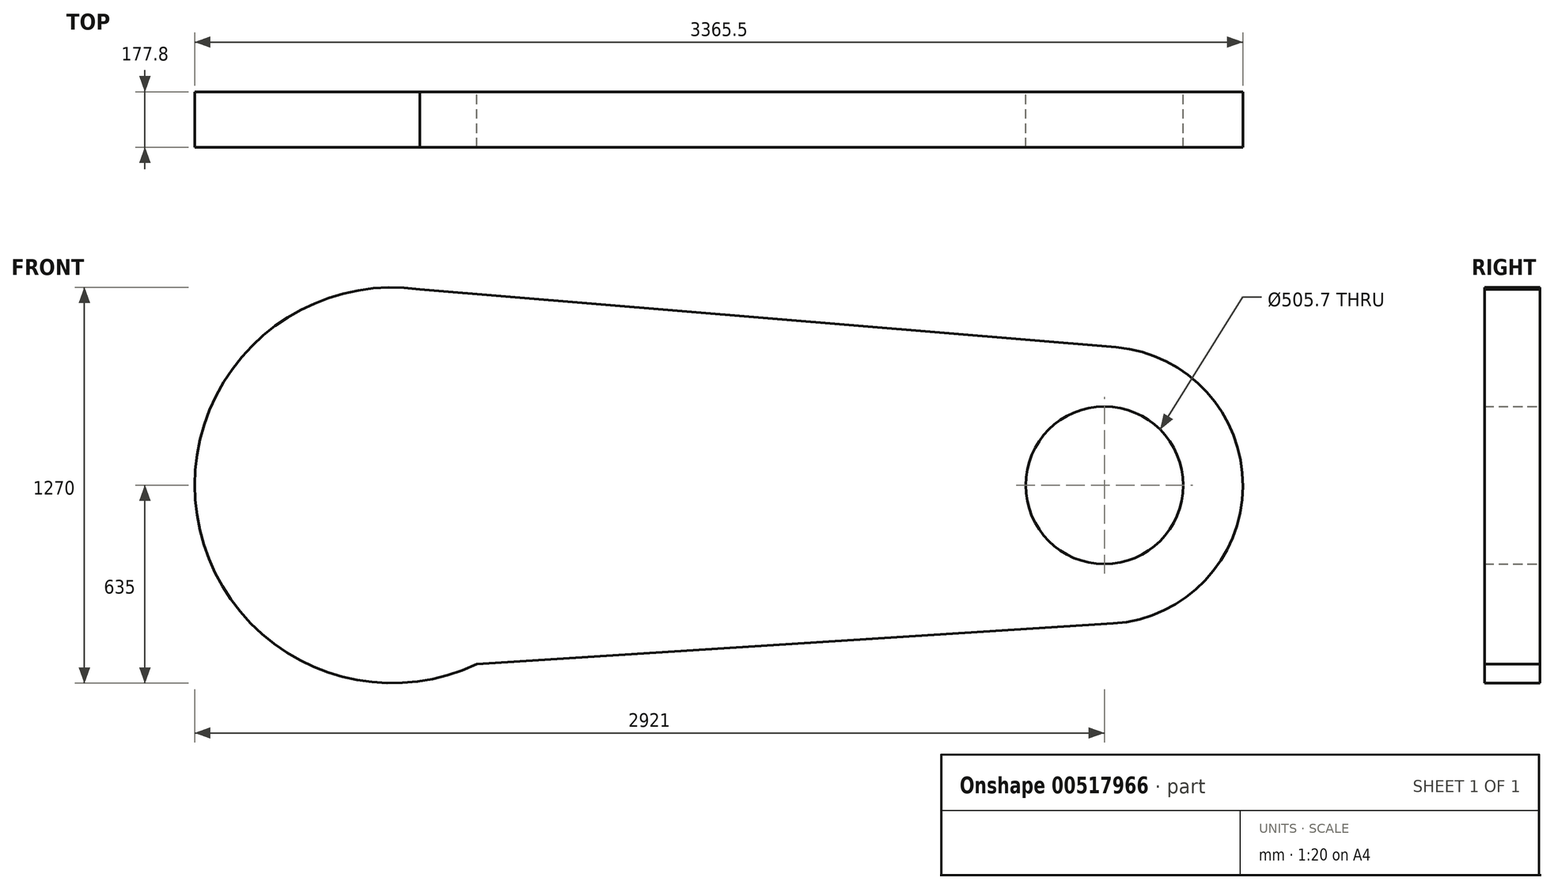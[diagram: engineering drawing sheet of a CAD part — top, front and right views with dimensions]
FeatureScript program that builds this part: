
annotation { "Feature Type Name" : "Feature", "Feature Type Description" : "" }
export const myFeature = defineFeature(function(context is Context, id is Id, definition is map)
    precondition{}
    {
        {
            var Q0;
            Q0=qCreatedBy(makeId("Front.planeOp"),FACE);
            var sketch = newSketch(context, id + "F0", { "sketchPlane" : qUnion([Q0])});
            skCircle(sketch, "E0", {"center": v(0, 0) * mm, "radius": 635 * mm});
            skCircle(sketch, "E1", {"center": v(2286, 0) * mm, "radius": 444.5 * mm});
            skLineSegment(sketch, "E2", {"start": v(87.46, 628.95) * mm, "end": v(2322.85, 442.97) * mm});
            skLineSegment(sketch, "E3", {"start": v(-195.16, -604.27) * mm, "end": v(2314.4, -443.6) * mm});
            skCircle(sketch, "E4", {"center": v(0, 0) * mm, "radius": 355.7 * mm});
            skCircle(sketch, "E5", {"center": v(2300.06, -19.76) * mm, "radius": 24.25 * mm});
            skCircle(sketch, "E6", {"center": v(2286, 0) * mm, "radius": 252.85 * mm});
            skSolve(sketch);
        }
        {
            var Q0;
            Q0 = qSketchRegion(id + "F0", true);
            var Q1;
            Q1=makeQuery(id+"F0.imprint","IMPRINT",FACE,{"disambiguationData":[TD([[makeQuery(id+"F0.imprint","IMPRINT",EDGE,{"derivedFrom":sQuery(id+"F0.wireOp",EDGE,"E4")}),1.0]])]});
            extrude(context, id + "F1", {"entities" : qUnion([Q0, Q1]), "depth" : 50.8 * mm, "offsetDistance" : 25.4 * mm});
        }
        {
            var Q0;
            Q0=makeQuery(id+"F1.opExtrude","CAP_FACE",FACE,{"disambiguationData":[OSD([sQuery(id+"F0.wireOp",EDGE,"E0"),sQuery(id+"F0.wireOp",EDGE,"E2"),sQuery(id+"F0.wireOp",EDGE,"E3"),sQuery(id+"F0.wireOp",EDGE,"E1"),sQuery(id+"F0.wireOp",EDGE,"E6")])],"isStart":false});
            extrude(context, id + "F2", {"entities" : qUnion([Q0]), "operationType" : NewBodyOperationType.ADD, "depth" : 127 * mm, "offsetDistance" : 25.4 * mm});
        }
    });
